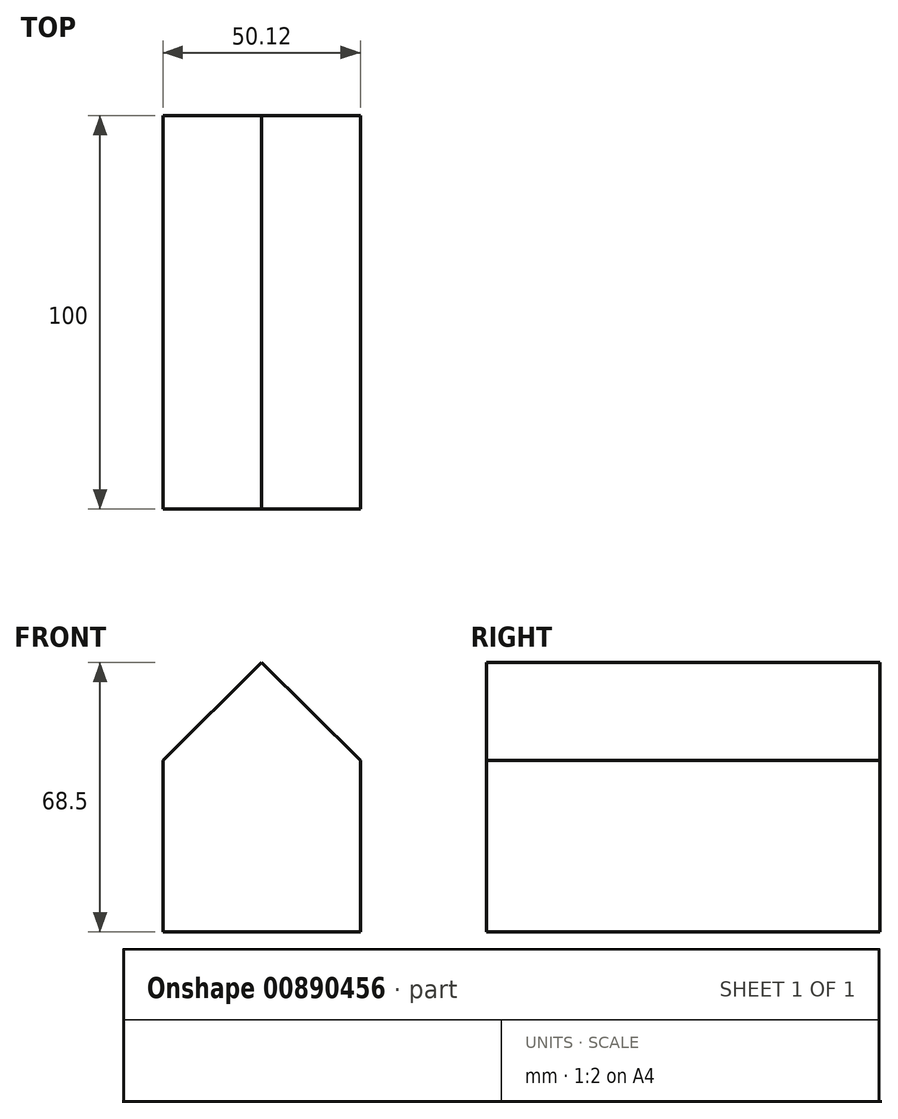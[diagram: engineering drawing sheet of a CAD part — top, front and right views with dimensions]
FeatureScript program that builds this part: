
annotation { "Feature Type Name" : "Feature", "Feature Type Description" : "" }
export const myFeature = defineFeature(function(context is Context, id is Id, definition is map)
    precondition{}
    {
        {
            var Q0;
            Q0=qCreatedBy(makeId("Front.planeOp"),FACE);
            var sketch = newSketch(context, id + "F0", { "sketchPlane" : qUnion([Q0])});
            skLineSegment(sketch, "E0.bottom", {"start": v(0, 0) * mm, "end": v(50.12, 0) * mm});
            skLineSegment(sketch, "E0.left", {"start": v(0, 0) * mm, "end": v(0, 43.61) * mm});
            skLineSegment(sketch, "E0.right", {"start": v(50.12, 0) * mm, "end": v(50.12, 43.61) * mm});
            skLineSegment(sketch, "E1", {"start": v(25.06, 68.5) * mm, "end": v(0, 43.61) * mm});
            skLineSegment(sketch, "E2", {"start": v(25.06, 68.5) * mm, "end": v(50.12, 43.61) * mm});
            skPoint(sketch, "E3.start.orphan", {"position": v(25.06, 43.61) * mm});
            skSolve(sketch);
        }
        {
            var Q0;
            Q0 = qSketchRegion(id + "F0", true);
            extrude(context, id + "F1", {"entities" : qUnion([Q0]), "depth" : 100 * mm, "offsetDistance" : 25.4 * mm});
        }
    });
